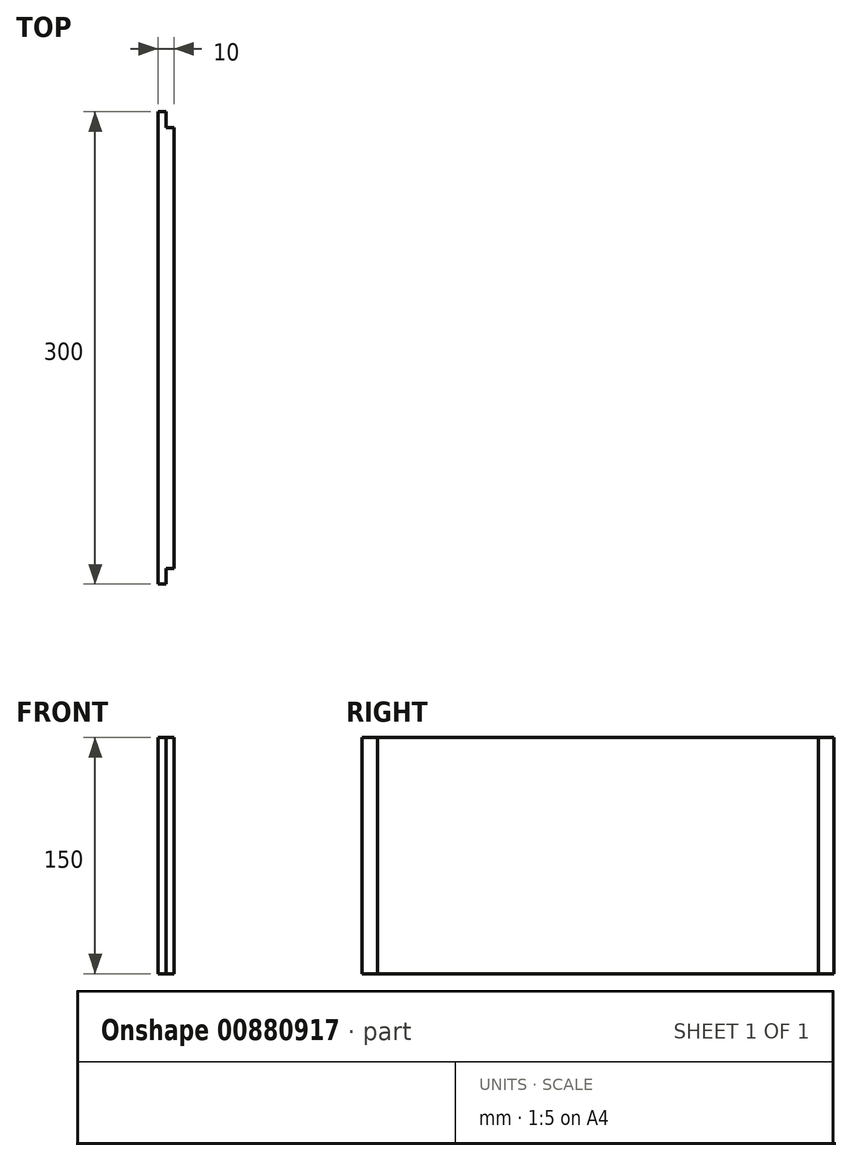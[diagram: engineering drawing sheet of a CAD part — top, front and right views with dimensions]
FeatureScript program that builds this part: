
annotation { "Feature Type Name" : "Feature", "Feature Type Description" : "" }
export const myFeature = defineFeature(function(context is Context, id is Id, definition is map)
    precondition{}
    {
        {
            var Q0;
            Q0=qCreatedBy(makeId("Top.planeOp"),FACE);
            var sketch = newSketch(context, id + "F0", { "sketchPlane" : qUnion([Q0])});
            skLineSegment(sketch, "E0.bottom", {"start": v(-6, 75) * mm, "end": v(0, 75) * mm});
            skLineSegment(sketch, "E0.top", {"start": v(-6, -75) * mm, "end": v(0, -75) * mm});
            skLineSegment(sketch, "E0.left", {"start": v(-6, 75) * mm, "end": v(-6, -75) * mm});
            skLineSegment(sketch, "E0.right", {"start": v(6, 63) * mm, "end": v(6, -63) * mm});
            skPoint(sketch, "E0.middle", {"position": v(0, 0) * mm});
            skLineSegment(sketch, "E1", {"start": v(0, 75) * mm, "end": v(0, 63) * mm});
            skLineSegment(sketch, "E2", {"start": v(0, -75) * mm, "end": v(0, -63) * mm});
            skLineSegment(sketch, "E3", {"start": v(0, -63) * mm, "end": v(6, -63) * mm});
            skPoint(sketch, "E4.orphan", {"position": v(6, -75) * mm});
            skLineSegment(sketch, "E5", {"start": v(0, 63) * mm, "end": v(6, 63) * mm});
            skPoint(sketch, "E6.orphan", {"position": v(6, 75) * mm});
            skSolve(sketch);
        }
        {
            var Q0;
            Q0=makeQuery(id+"F0.imprint","IMPRINT",FACE,{"disambiguationData":[TD([[makeQuery(id+"F0.imprint","IMPRINT",EDGE,{"derivedFrom":sQuery(id+"F0.wireOp",EDGE,"E0.bottom")}),-1.0]])]});
            extrude(context, id + "F1", {"entities" : qUnion([Q0]), "depth" : 150 * mm, "offsetDistance" : 25 * mm});
        }
        {
            var Q0;
            Q0=makeQuery(id+"F1.opExtrude","SWEPT_BODY",BODY,{"disambiguationData":[OSD([sQuery(id+"F0.wireOp",EDGE,"E0.bottom"),sQuery(id+"F0.wireOp",EDGE,"E0.top"),sQuery(id+"F0.wireOp",EDGE,"E0.left"),sQuery(id+"F0.wireOp",EDGE,"E0.right"),sQuery(id+"F0.wireOp",EDGE,"E1"),sQuery(id+"F0.wireOp",EDGE,"E2"),sQuery(id+"F0.wireOp",EDGE,"E3"),sQuery(id+"F0.wireOp",EDGE,"E5")])]});
            deleteBodies(context, id + "F2", {"entities" : qUnion([Q0])});
        }
        {
            var Q0;
            Q0=qCreatedBy(makeId("Top.planeOp"),FACE);
            var sketch = newSketch(context, id + "F3", { "sketchPlane" : qUnion([Q0])});
            skLineSegment(sketch, "E7.bottom", {"start": v(0, 150) * mm, "end": v(-5, 150) * mm});
            skLineSegment(sketch, "E7.top", {"start": v(0, -150) * mm, "end": v(-5, -150) * mm});
            skLineSegment(sketch, "E7.left", {"start": v(5, 140) * mm, "end": v(5, -140) * mm});
            skLineSegment(sketch, "E7.right", {"start": v(-5, 150) * mm, "end": v(-5, -150) * mm});
            skPoint(sketch, "E7.middle", {"position": v(0, 0) * mm});
            skLineSegment(sketch, "E8", {"start": v(0, 150) * mm, "end": v(0, 140) * mm});
            skLineSegment(sketch, "E9", {"start": v(0, 140) * mm, "end": v(5, 140) * mm});
            skPoint(sketch, "E10.orphan", {"position": v(5, 150) * mm});
            skLineSegment(sketch, "E11", {"start": v(0, -150) * mm, "end": v(0, -140) * mm});
            skLineSegment(sketch, "E12", {"start": v(5, -140) * mm, "end": v(0, -140) * mm});
            skPoint(sketch, "E13.orphan", {"position": v(5, -150) * mm});
            skSolve(sketch);
        }
        {
            var Q0;
            Q0=makeQuery(id+"F3.imprint","IMPRINT",FACE,{"disambiguationData":[TD([[makeQuery(id+"F3.imprint","IMPRINT",EDGE,{"derivedFrom":sQuery(id+"F3.wireOp",EDGE,"E7.bottom")}),1.0]])]});
            extrude(context, id + "F4", {"entities" : qUnion([Q0]), "depth" : 150 * mm, "offsetDistance" : 25 * mm});
        }
    });
